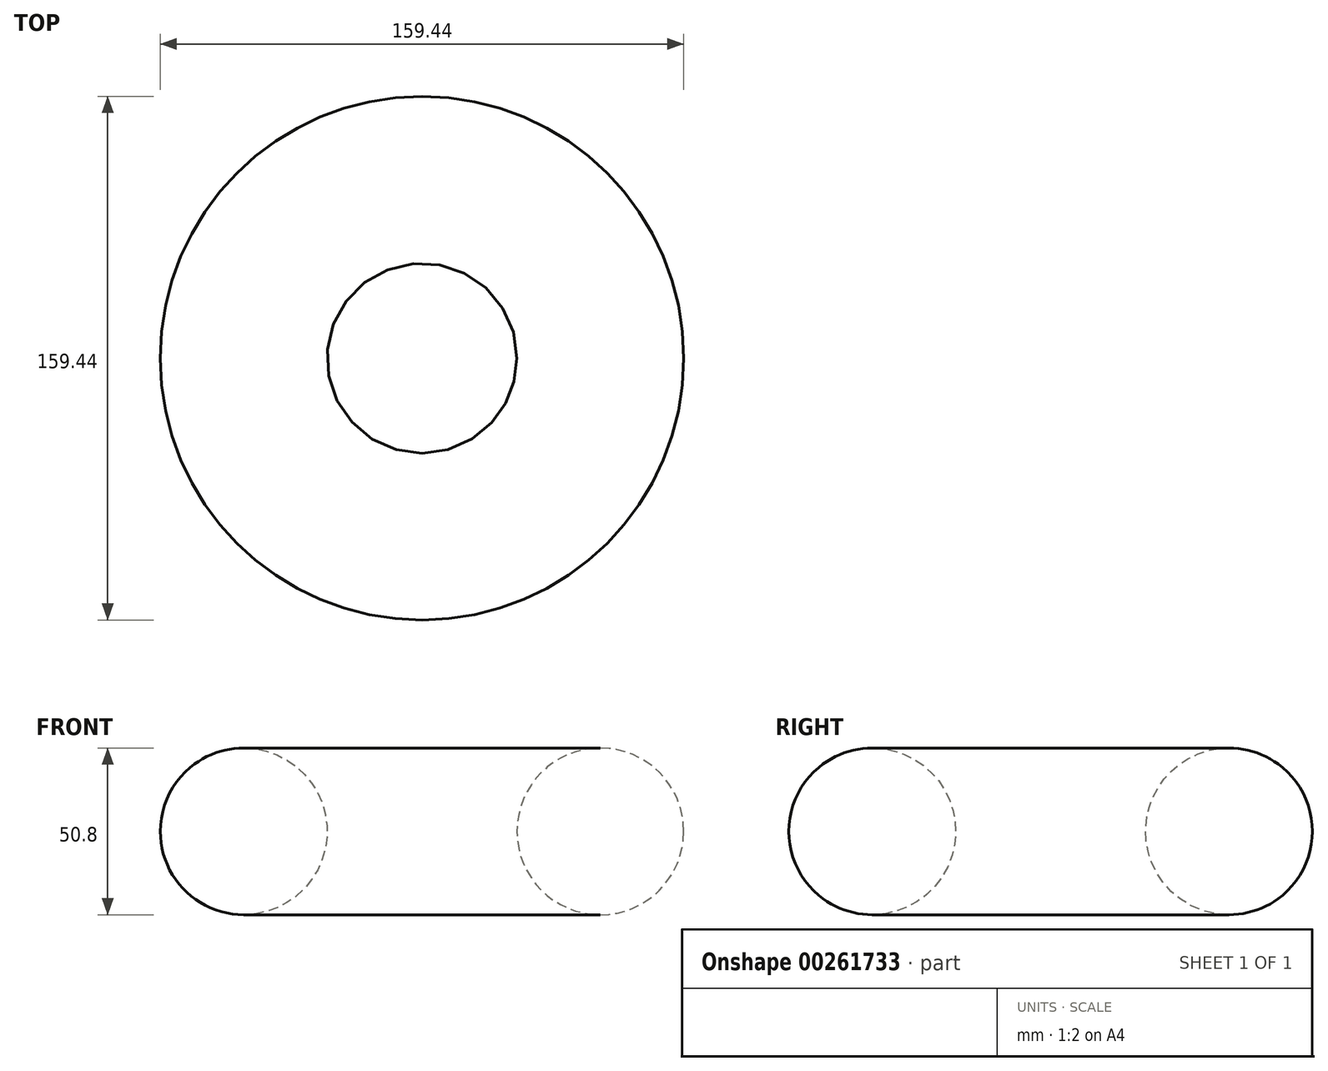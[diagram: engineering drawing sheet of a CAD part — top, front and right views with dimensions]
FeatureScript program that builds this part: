
annotation { "Feature Type Name" : "Feature", "Feature Type Description" : "" }
export const myFeature = defineFeature(function(context is Context, id is Id, definition is map)
    precondition{}
    {
        {
            var Q0;
            Q0=qCreatedBy(makeId("Front.planeOp"),FACE);
            var sketch = newSketch(context, id + "F0", { "sketchPlane" : qUnion([Q0])});
            skCircle(sketch, "E0", {"center": v(-54.32, 0) * mm, "radius": 25.4 * mm});
            skLineSegment(sketch, "E1", {"start": v(0, 53.3) * mm, "end": v(0, -48.3) * mm, "construction": true});
            skSolve(sketch);
        }
        {
            var Q0;
            Q0=makeQuery(id+"F0.imprint","IMPRINT",FACE,{"disambiguationData":[TD([[makeQuery(id+"F0.imprint","IMPRINT",EDGE,{"derivedFrom":sQuery(id+"F0.wireOp",EDGE,"E0")}),1.0]])]});
            var Q1;
            Q1=sQuery(id+"F0.wireOp",EDGE,"E1");
            revolve(context, id + "F1", {"entities" : qUnion([Q0]), "axis" : qUnion([Q1]), "revolveType" : RevolveType.FULL});
        }
    });
